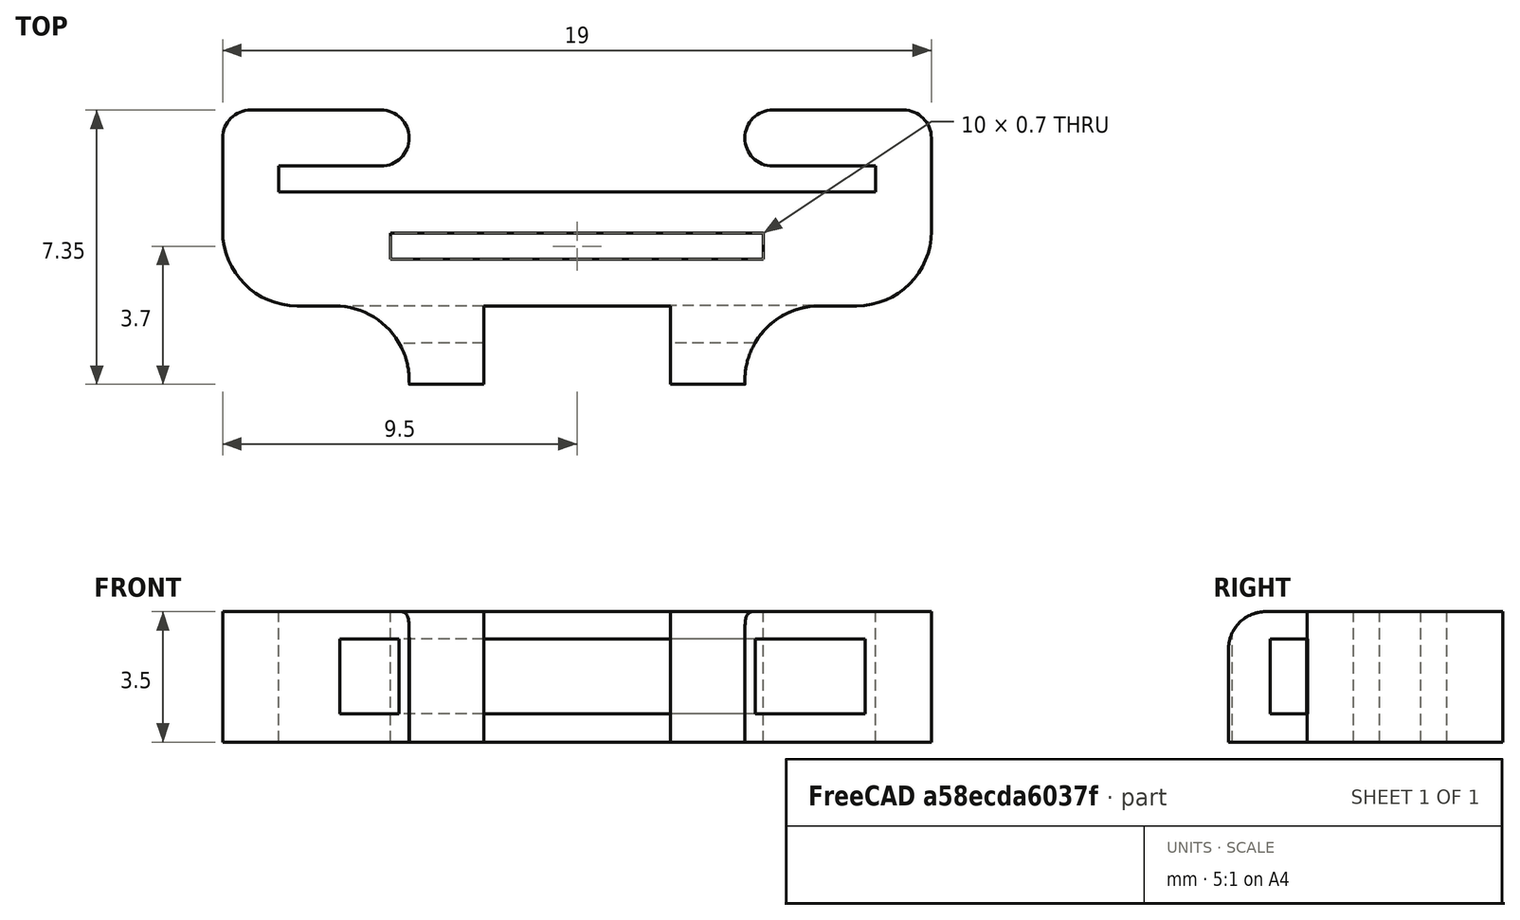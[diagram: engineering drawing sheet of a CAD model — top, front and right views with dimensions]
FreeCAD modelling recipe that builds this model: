
FCSTD DOCUMENT  (FreeCAD 1.0R38641 +468 (Git))
Label: tof_cable_management
License: All rights reserved
LicenseURL: https://en.wikipedia.org/wiki/All_rights_reserved
objects: Sketcher::SketchObject×2, PartDesign::Pad×1, PartDesign::Plane×1, PartDesign::Pocket×1, PartDesign::Fillet×1, PartDesign::Body×1
note: 15 computed .brp shape members not serialized (recipe doc carries the construction recipe); baked Part::Feature solids carry a one-line shape summary decoded from their .brp

FEATURE [Sketcher::SketchObject] Sketch
  ArcFitTolerance = 1e-06
  FullyConstrained = false
  MakeInternals = false
  sketch-geometry (32):
    g0: LineSegment StartX=135 StartY=79.75 StartZ=0 EndX=145 EndY=79.75 EndZ=0
    g1: LineSegment StartX=145 StartY=79.75 StartZ=0 EndX=145 EndY=80.45 EndZ=0
    g2: LineSegment StartX=135 StartY=80.45 StartZ=0 EndX=135 EndY=79.75 EndZ=0
    g3: LineSegment StartX=148 StartY=81.55 StartZ=0 EndX=148 EndY=82.25 EndZ=0
    g4: LineSegment StartX=148 StartY=82.25 StartZ=0 EndX=145.25 EndY=82.25 EndZ=0
    g5: LineSegment StartX=132 StartY=82.25 StartZ=0 EndX=132 EndY=81.55 EndZ=0
    g6: LineSegment StartX=132 StartY=82.25 StartZ=0 EndX=134.75 EndY=82.25 EndZ=0
    g7: LineSegment StartX=130.5 StartY=83 StartZ=0 EndX=130.5 EndY=80.5 EndZ=0
    g8: LineSegment StartX=149.5 StartY=80.5 StartZ=0 EndX=149.5 EndY=83 EndZ=0
    g9: LineSegment StartX=148.75 StartY=83.75 StartZ=0 EndX=145.25 EndY=83.75 EndZ=0
    g10: LineSegment StartX=131.25 StartY=83.75 StartZ=0 EndX=134.75 EndY=83.75 EndZ=0
    g11: ArcOfCircle CenterX=131.25 CenterY=83 CenterZ=0 NormalX=0 NormalY=0 NormalZ=1 AngleXU=0 Radius=0.75 StartAngle=1.5708 EndAngle=3.14159
    g12: ArcOfCircle CenterX=148.75 CenterY=83 CenterZ=0 NormalX=0 NormalY=0 NormalZ=1 AngleXU=0 Radius=0.75 StartAngle=0 EndAngle=1.5708
    g13: ArcOfCircle CenterX=134.75 CenterY=83 CenterZ=0 NormalX=0 NormalY=0 NormalZ=1 AngleXU=0 Radius=0.75 StartAngle=0 EndAngle=1.5708
    g14: ArcOfCircle CenterX=145.25 CenterY=83 CenterZ=0 NormalX=0 NormalY=0 NormalZ=1 AngleXU=0 Radius=0.75 StartAngle=1.5708 EndAngle=3.14159
    g15: ArcOfCircle CenterX=145.25 CenterY=83 CenterZ=0 NormalX=0 NormalY=0 NormalZ=1 AngleXU=0 Radius=0.75 StartAngle=3.14159 EndAngle=4.71239
    g16: ArcOfCircle CenterX=134.75 CenterY=83 CenterZ=0 NormalX=0 NormalY=0 NormalZ=1 AngleXU=0 Radius=0.75 StartAngle=4.71239 EndAngle=6.28319
    g17: LineSegment StartX=132 StartY=81.55 StartZ=0 EndX=148 EndY=81.55 EndZ=0
    g18: LineSegment StartX=145 StartY=80.45 StartZ=0 EndX=135 EndY=80.45 EndZ=0
    g19: LineSegment StartX=142.5 StartY=76.3959 StartZ=0 EndX=142.5 EndY=78.5 EndZ=0
    g20: LineSegment StartX=142.5 StartY=78.5 StartZ=0 EndX=137.5 EndY=78.5 EndZ=0
    g21: LineSegment StartX=137.5 StartY=78.5 StartZ=0 EndX=137.503 EndY=76.3959 EndZ=0
    g22: LineSegment StartX=144.5 StartY=76.3959 StartZ=0 EndX=144.5 EndY=76.5 EndZ=0
    g23: LineSegment StartX=135.5 StartY=76.5 StartZ=0 EndX=135.503 EndY=76.3959 EndZ=0
    g24: LineSegment StartX=146.5 StartY=78.5 StartZ=0 EndX=147.5 EndY=78.5 EndZ=0
    g25: LineSegment StartX=133.5 StartY=78.5 StartZ=0 EndX=132.5 EndY=78.5 EndZ=0
    g26: LineSegment StartX=142.5 StartY=76.3959 StartZ=0 EndX=144.5 EndY=76.3959 EndZ=0
    g27: LineSegment StartX=135.503 StartY=76.3959 StartZ=0 EndX=137.503 EndY=76.3959 EndZ=0
    g28: ArcOfCircle CenterX=147.5 CenterY=80.5 CenterZ=0 NormalX=0 NormalY=0 NormalZ=1 AngleXU=0 Radius=2 StartAngle=4.71239 EndAngle=6.28319
    g29: ArcOfCircle CenterX=132.5 CenterY=80.5 CenterZ=0 NormalX=0 NormalY=0 NormalZ=1 AngleXU=0 Radius=2 StartAngle=3.14159 EndAngle=4.71239
    g30: ArcOfCircle CenterX=133.5 CenterY=76.5 CenterZ=0 NormalX=0 NormalY=0 NormalZ=1 AngleXU=0 Radius=2 StartAngle=0 EndAngle=1.5708
    g31: ArcOfCircle CenterX=146.5 CenterY=76.5 CenterZ=0 NormalX=0 NormalY=0 NormalZ=1 AngleXU=0 Radius=2 StartAngle=1.5708 EndAngle=3.14159
  constraints (7):
    c: Coincident(g23,g27)
    c: Coincident(g21,g27)
    c: Coincident(g19,g26)
    c: Coincident(g22,g26)
    c: Horizontal(g21,g19)
    c: Horizontal(g27)
    c: Horizontal(g26)
FEATURE [PartDesign::Pad] Pad
  Direction = (0,0,1)
  Length = 3.5
  Length2 = 10
  Profile = -> Sketch
  ReferenceAxis = -> Sketch [N_Axis]
  Refine = true
  Suppressed = false
  Type = 0
FEATURE [PartDesign::Plane] DatumPlane
  AttachmentSupport = -> [Pad]
  Length = 123.742
  MapMode = 5
  Placement = pos=(137.603,0.180629,0) rot=(0.576845,0.577603,0.577603;2.09515rad)
  ResizeMode = 0
  Width = 64.7634
FEATURE [Sketcher::SketchObject] Sketch001
  ArcFitTolerance = 1e-06
  AttachmentSupport = -> [DatumPlane]
  ExternalGeometry = -> [Pad]
  FullyConstrained = false
  MakeInternals = false
  MapMode = 5
  Placement = pos=(137.603,0.180629,0) rot=(0.576845,0.577603,0.577603;2.09515rad)
  sketch-geometry (4):
    g0: LineSegment StartX=77.3194 StartY=2.76189 StartZ=0 EndX=77.3194 EndY=0.76189 EndZ=0
    g1: LineSegment StartX=77.3194 StartY=0.76189 StartZ=0 EndX=78.3194 EndY=0.76189 EndZ=0
    g2: LineSegment StartX=78.3194 StartY=0.76189 StartZ=0 EndX=78.3194 EndY=2.76189 EndZ=0
    g3: LineSegment StartX=78.3194 StartY=2.76189 StartZ=0 EndX=77.3194 EndY=2.76189 EndZ=0
  constraints (11):
    c: Coincident(g0,g1)
    c: Coincident(g1,g2)
    c: Coincident(g2,g3)
    c: Coincident(g3,g0)
    c: Vertical(g0)
    c: Vertical(g2)
    c: Horizontal(g1)
    c: Horizontal(g3)
    c: DistanceY(g0,g0) = 2
    c: DistanceX(g1,g1) = 1
    c: Vertical(g3,g-4)
FEATURE [PartDesign::Pocket] Pocket
  BaseFeature = -> Pad
  Direction = (-0.999999,-0.00131268,0)
  Length = 5
  Length2 = 5
  Midplane = true
  Profile = -> Sketch001
  ReferenceAxis = -> Sketch001 [N_Axis]
  Refine = true
  Suppressed = false
  Type = 1
FEATURE [PartDesign::Fillet] Fillet
  Base = -> Pocket [Edge51,Edge55]
  BaseFeature = -> Pocket
  Radius = 1
  Refine = true
  SupportTransform = false
  Suppressed = false
  UseAllEdges = false
FEATURE [PartDesign::Body] Body
  AllowCompound = false
  Group = -> [Sketch,Pad,DatumPlane,Sketch001,Pocket,Fillet]
  Origin = -> Origin
  Tip = -> Fillet
